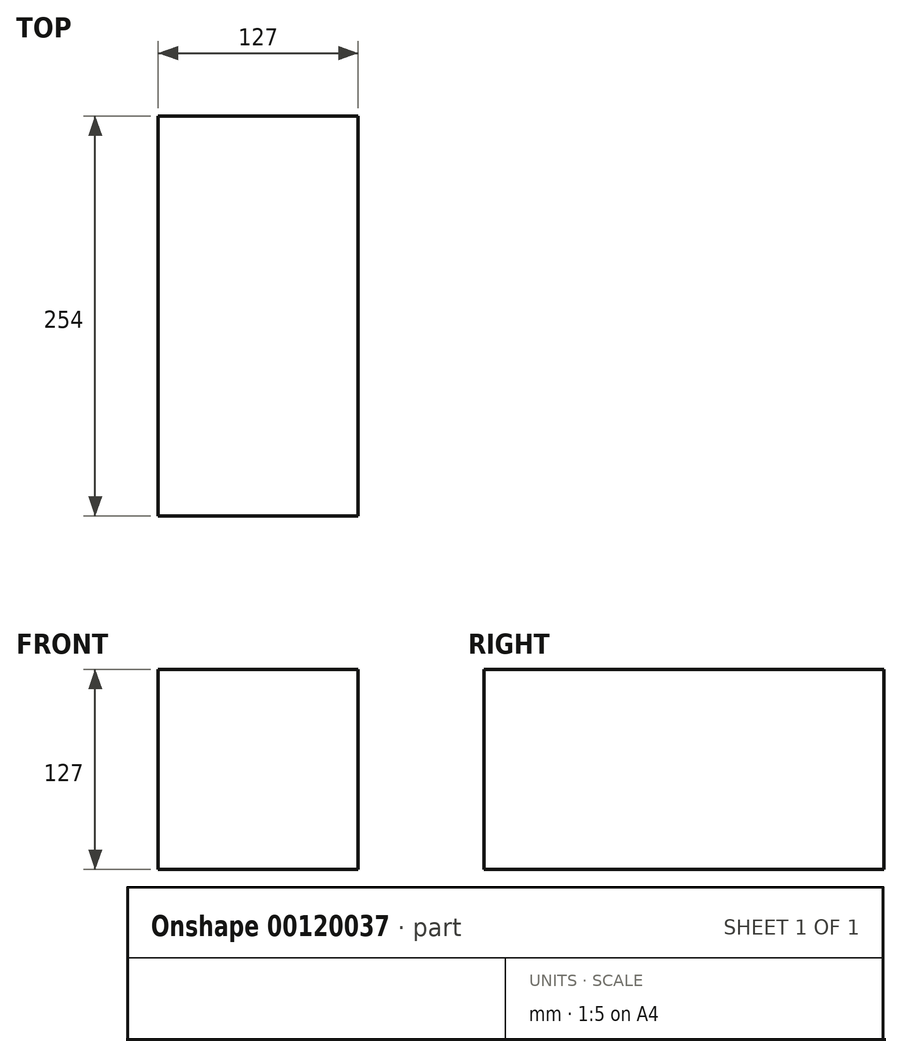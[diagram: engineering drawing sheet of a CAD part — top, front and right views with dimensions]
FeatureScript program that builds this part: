
annotation { "Feature Type Name" : "Feature", "Feature Type Description" : "" }
export const myFeature = defineFeature(function(context is Context, id is Id, definition is map)
    precondition{}
    {
        {
            var Q0;
            Q0=qCreatedBy(makeId("Front.planeOp"),FACE);
            var sketch = newSketch(context, id + "F0", { "sketchPlane" : qUnion([Q0])});
            skLineSegment(sketch, "E0", {"start": v(0, 0) * mm, "end": v(0, 127) * mm});
            skLineSegment(sketch, "E1", {"start": v(0, 127) * mm, "end": v(127, 127) * mm});
            skLineSegment(sketch, "E2", {"start": v(127, 127) * mm, "end": v(127, 0) * mm});
            skLineSegment(sketch, "E3", {"start": v(127, 0) * mm, "end": v(0, 0) * mm});
            skSolve(sketch);
        }
        {
            var Q0;
            Q0 = qSketchRegion(id + "F0", true);
            extrude(context, id + "F1", {"entities" : qUnion([Q0]), "oppositeDirection" : true, "depth" : 254 * mm});
        }
    });
